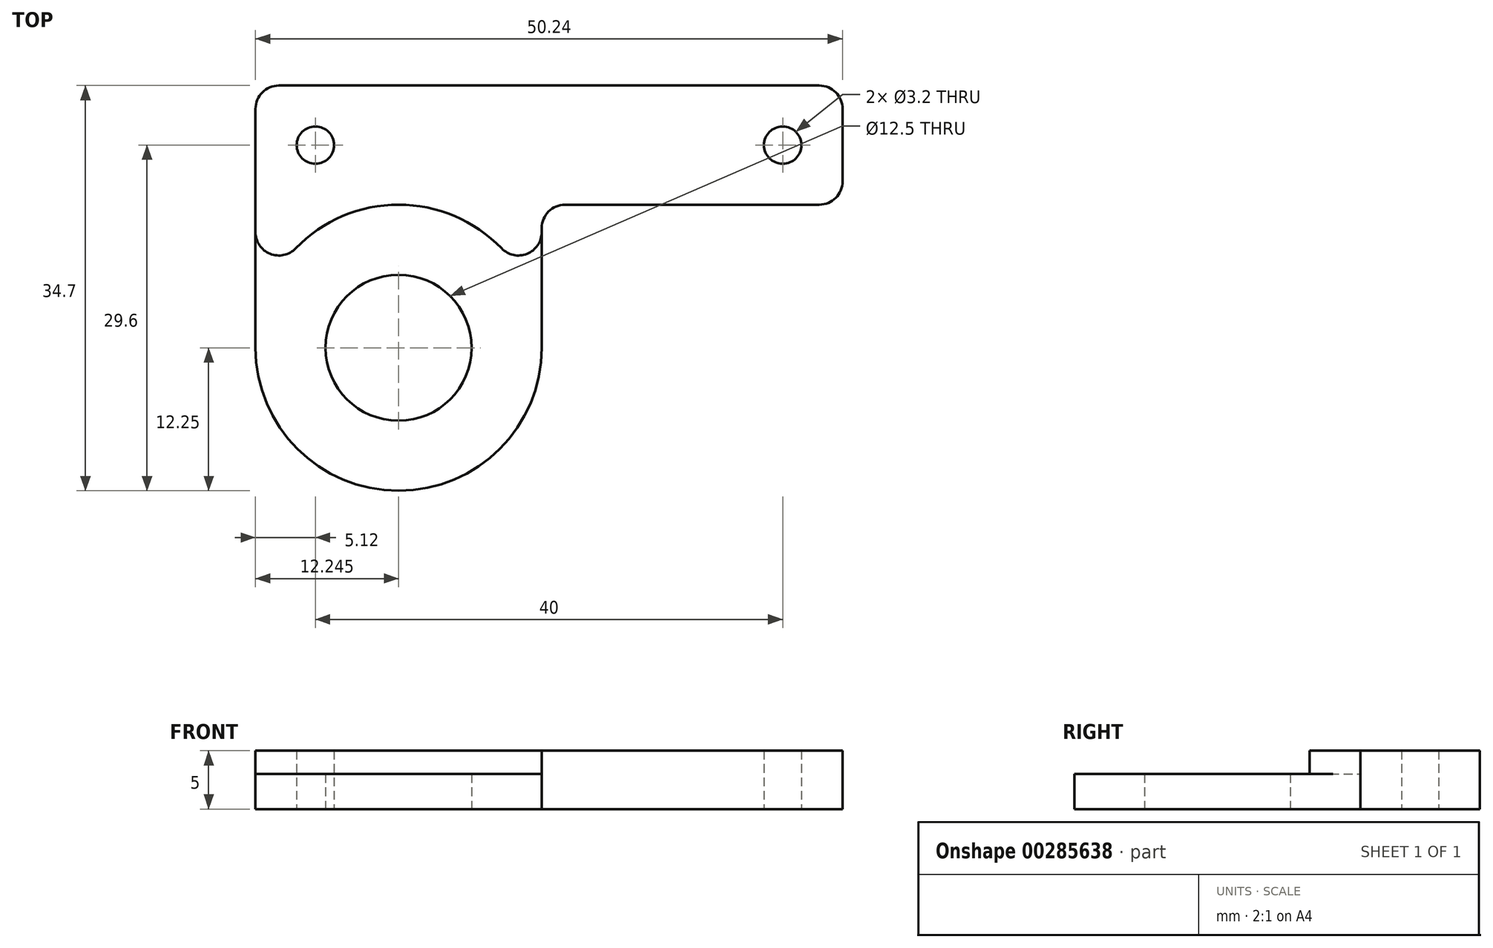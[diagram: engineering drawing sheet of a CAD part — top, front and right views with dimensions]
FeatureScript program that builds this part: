
annotation { "Feature Type Name" : "Feature", "Feature Type Description" : "" }
export const myFeature = defineFeature(function(context is Context, id is Id, definition is map)
    precondition{}
    {
        {
            var Q0;
            Q0=qCreatedBy(makeId("Top.planeOp"),FACE);
            var sketch = newSketch(context, id + "F0", { "sketchPlane" : qUnion([Q0])});
            skCircle(sketch, "E0", {"center": v(-20, 0) * mm, "radius": 1.6 * mm});
            skCircle(sketch, "E1", {"center": v(20, 0) * mm, "radius": 1.6 * mm});
            skLineSegment(sketch, "E2.bottom", {"start": v(25.12, 5.1) * mm, "end": v(-25.12, 5.1) * mm, "construction": true});
            skLineSegment(sketch, "E2.top", {"start": v(25.12, -5.1) * mm, "end": v(-25.12, -5.1) * mm, "construction": true});
            skLineSegment(sketch, "E2.left", {"start": v(25.12, 5.1) * mm, "end": v(25.12, -5.1) * mm, "construction": true});
            skLineSegment(sketch, "E2.right", {"start": v(-25.12, 5.1) * mm, "end": v(-25.12, -5.1) * mm, "construction": true});
            skPoint(sketch, "E2.middle", {"position": v(0, 0) * mm});
            skCircle(sketch, "E3", {"center": v(-12.87, -17.35) * mm, "radius": 6.25 * mm});
            skCircle(sketch, "E4", {"center": v(-12.87, -17.35) * mm, "radius": 12.25 * mm, "construction": true});
            skLineSegment(sketch, "E5", {"start": v(-25.12, 5.1) * mm, "end": v(-25.12, -17.35) * mm});
            skArc(sketch, "E6", {"start": v(-25.12, -17.35) * mm, "mid": v(-12.87, -29.6) * mm, "end": v(-0.62, -17.35) * mm});
            skLineSegment(sketch, "E7", {"start": v(-0.62, -17.35) * mm, "end": v(-0.62, -5.1) * mm});
            skLineSegment(sketch, "E8", {"start": v(-0.62, -5.1) * mm, "end": v(25.12, -5.1) * mm});
            skLineSegment(sketch, "E9", {"start": v(25.12, 5.1) * mm, "end": v(-25.12, 5.1) * mm});
            skLineSegment(sketch, "E10", {"start": v(25.12, 5.1) * mm, "end": v(25.12, -5.1) * mm});
            skSolve(sketch);
        }
        {
            var Q0;
            Q0 = qSketchRegion(id + "F0", true);
            extrude(context, id + "F1", {"entities" : qUnion([Q0]), "depth" : 5 * mm});
        }
        {
            var Q0;
            Q0=makeQuery(id+"F1.opExtrude","CAP_FACE",FACE,{"disambiguationData":[OSD([sQuery(id+"F0.wireOp",EDGE,"E0"),sQuery(id+"F0.wireOp",EDGE,"E1"),sQuery(id+"F0.wireOp",EDGE,"E3"),sQuery(id+"F0.wireOp",EDGE,"E5"),sQuery(id+"F0.wireOp",EDGE,"E6"),sQuery(id+"F0.wireOp",EDGE,"E7"),sQuery(id+"F0.wireOp",EDGE,"E8"),sQuery(id+"F0.wireOp",EDGE,"E9"),sQuery(id+"F0.wireOp",EDGE,"E10")])],"isStart":false});
            var sketch = newSketch(context, id + "F2", { "sketchPlane" : qUnion([Q0])});
            skCircle(sketch, "E11", {"center": v(-12.87, -17.35) * mm, "radius": 11.25 * mm, "construction": true});
            skCircle(sketch, "E12", {"center": v(-12.87, -17.35) * mm, "radius": 12.25 * mm});
            skSolve(sketch);
        }
        {
            var Q0;
            Q0 = qSketchRegion(id + "F2", true);
            extrude(context, id + "F3", {"entities" : qUnion([Q0]), "operationType" : NewBodyOperationType.REMOVE, "oppositeDirection" : true, "depth" : 2 * mm});
        }
        {
            var Q0;
            Q0=makeQuery(id+"F1.opExtrude","SWEPT_EDGE",EDGE,{"disambiguationData":[OSD([sQuery(id+"F0.wireOp",EDGE,"E5"),sQuery(id+"F0.wireOp",EDGE,"E9")])]});
            var Q1;
            Q1=makeQuery(id+"F1.opExtrude","SWEPT_EDGE",EDGE,{"disambiguationData":[OSD([sQuery(id+"F0.wireOp",EDGE,"E8"),sQuery(id+"F0.wireOp",EDGE,"E10")])]});
            var Q2;
            Q2=makeQuery(id+"F1.opExtrude","SWEPT_EDGE",EDGE,{"disambiguationData":[OSD([sQuery(id+"F0.wireOp",EDGE,"E9"),sQuery(id+"F0.wireOp",EDGE,"E10")])]});
            var Q3;
            Q3=makeQuery(id+"F1.opExtrude","SWEPT_EDGE",EDGE,{"disambiguationData":[OSD([sQuery(id+"F0.wireOp",EDGE,"E7"),sQuery(id+"F0.wireOp",EDGE,"E8")])]});
            var Q4;
            {var subQ0=sQuery(id+"F0.wireOp",EDGE,"E5");Q4=makeQuery(id+"F3.boolean.opBoolean","SPLIT",EDGE,{"disambiguationData":[topologyDisambiguationEdgeConnected([makeQuery(id+"F3.opExtrude","SWEPT_FACE",FACE,{"disambiguationData":[OSD([sQuery(id+"F2.wireOp",EDGE,"E12")])]})])],"derivedFrom":makeQuery(id+"F1.opExtrude","SWEPT_EDGE",EDGE,{"disambiguationData":[OSD([subQ0,sQuery(id+"F0.wireOp",EDGE,"E6")])]})});}
            var Q5;
            {var subQ0=sQuery(id+"F0.wireOp",EDGE,"E7");Q5=makeQuery(id+"F3.boolean.opBoolean","SPLIT",EDGE,{"disambiguationData":[topologyDisambiguationEdgeConnected([makeQuery(id+"F3.opExtrude","SWEPT_FACE",FACE,{"disambiguationData":[OSD([sQuery(id+"F2.wireOp",EDGE,"E12")])]})])],"derivedFrom":makeQuery(id+"F1.opExtrude","SWEPT_EDGE",EDGE,{"disambiguationData":[OSD([sQuery(id+"F0.wireOp",EDGE,"E6"),subQ0])]})});}
            fillet(context, id + "F4", {"entities" : qUnion([Q0, Q1, Q2, Q3, Q4, Q5]), "radius" : 2 * mm, "tangentPropagation" : true, "allowEdgeOverflow" : false});
        }
    });
